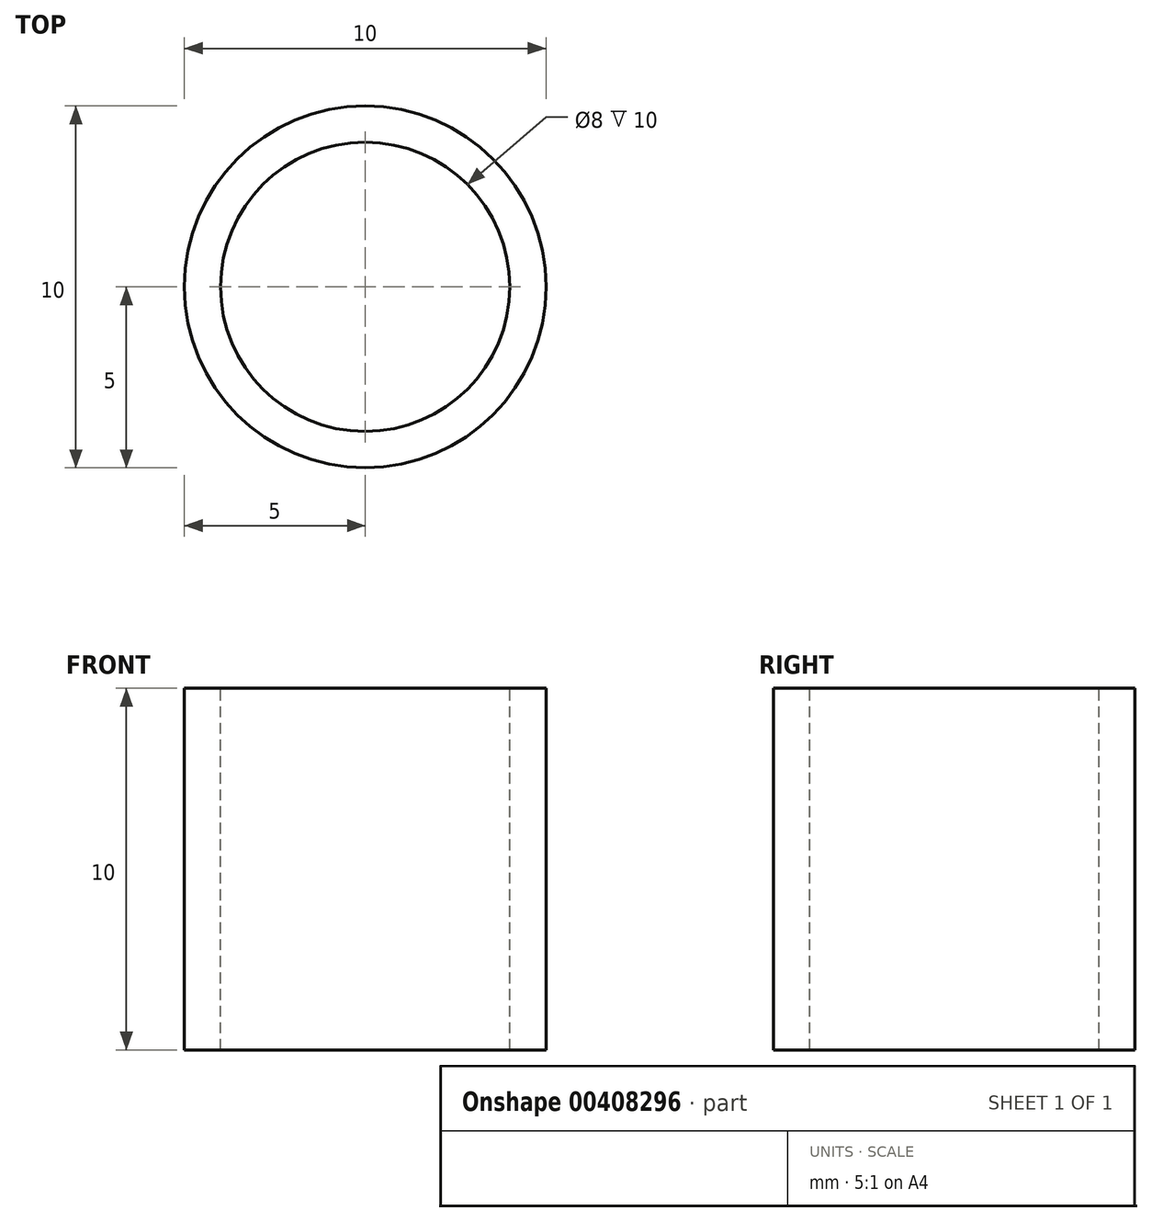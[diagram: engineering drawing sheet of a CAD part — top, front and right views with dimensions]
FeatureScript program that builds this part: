
annotation { "Feature Type Name" : "Feature", "Feature Type Description" : "" }
export const myFeature = defineFeature(function(context is Context, id is Id, definition is map)
    precondition{}
    {
        {
            var Q0;
            Q0=qCreatedBy(makeId("Front.planeOp"),FACE);
            var sketch = newSketch(context, id + "F0", { "sketchPlane" : qUnion([Q0])});
            skLineSegment(sketch, "E0.bottom", {"start": v(5, -5) * mm, "end": v(-5, -5) * mm});
            skLineSegment(sketch, "E0.top", {"start": v(5, 5) * mm, "end": v(-5, 5) * mm});
            skLineSegment(sketch, "E0.left", {"start": v(5, -5) * mm, "end": v(5, 5) * mm});
            skLineSegment(sketch, "E0.right", {"start": v(-5, -5) * mm, "end": v(-5, 5) * mm});
            skPoint(sketch, "E0.middle", {"position": v(0, 0) * mm});
            skLineSegment(sketch, "E1", {"start": v(4, 5) * mm, "end": v(4, -5) * mm});
            skLineSegment(sketch, "E2", {"start": v(0, 5) * mm, "end": v(0, -5) * mm});
            skLineSegment(sketch, "E3", {"start": v(-4, 5) * mm, "end": v(-4, -5) * mm});
            skSolve(sketch);
        }
        {
            var Q0;
            {var subQ0=sQuery(id+"F0.wireOp",EDGE,"E0.left");Q0=makeQuery(id+"F0.imprint","IMPRINT",FACE,{"disambiguationData":[TD([[makeQuery(id+"F0.imprint","IMPRINT",EDGE,{"derivedFrom":subQ0}),1.0]])]});}
            var Q1;
            Q1=sQuery(id+"F0.wireOp",EDGE,"E2");
            revolve(context, id + "F1", {"entities" : qUnion([Q0]), "axis" : qUnion([Q1]), "revolveType" : RevolveType.FULL});
        }
    });
